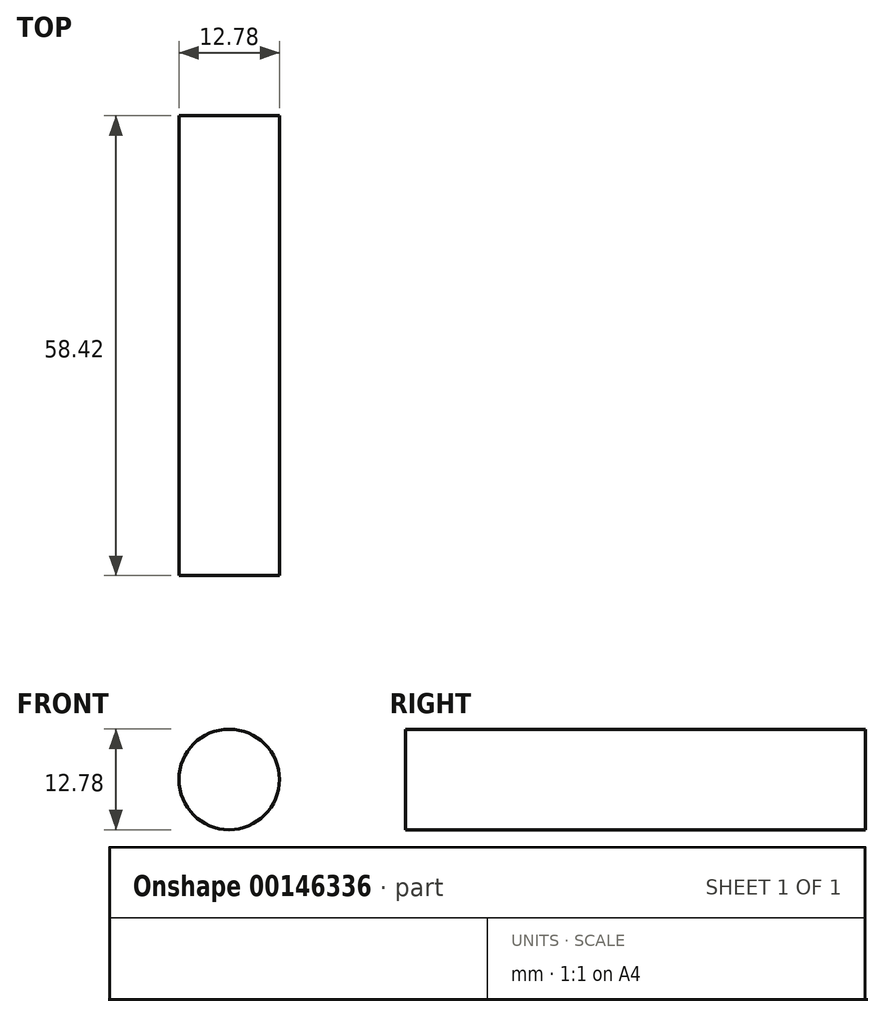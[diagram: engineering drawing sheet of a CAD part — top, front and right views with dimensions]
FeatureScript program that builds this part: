
annotation { "Feature Type Name" : "Feature", "Feature Type Description" : "" }
export const myFeature = defineFeature(function(context is Context, id is Id, definition is map)
    precondition{}
    {
        {
            var Q0;
            Q0=qCreatedBy(makeId("Front.planeOp"),FACE);
            var sketch = newSketch(context, id + "F0", { "sketchPlane" : qUnion([Q0])});
            skCircle(sketch, "E0", {"center": v(0, 0) * mm, "radius": 6.39 * mm});
            skSolve(sketch);
        }
        {
            var Q0;
            Q0 = qSketchRegion(id + "F0", true);
            extrude(context, id + "F1", {"entities" : qUnion([Q0]), "depth" : 58.42 * mm});
        }
    });
